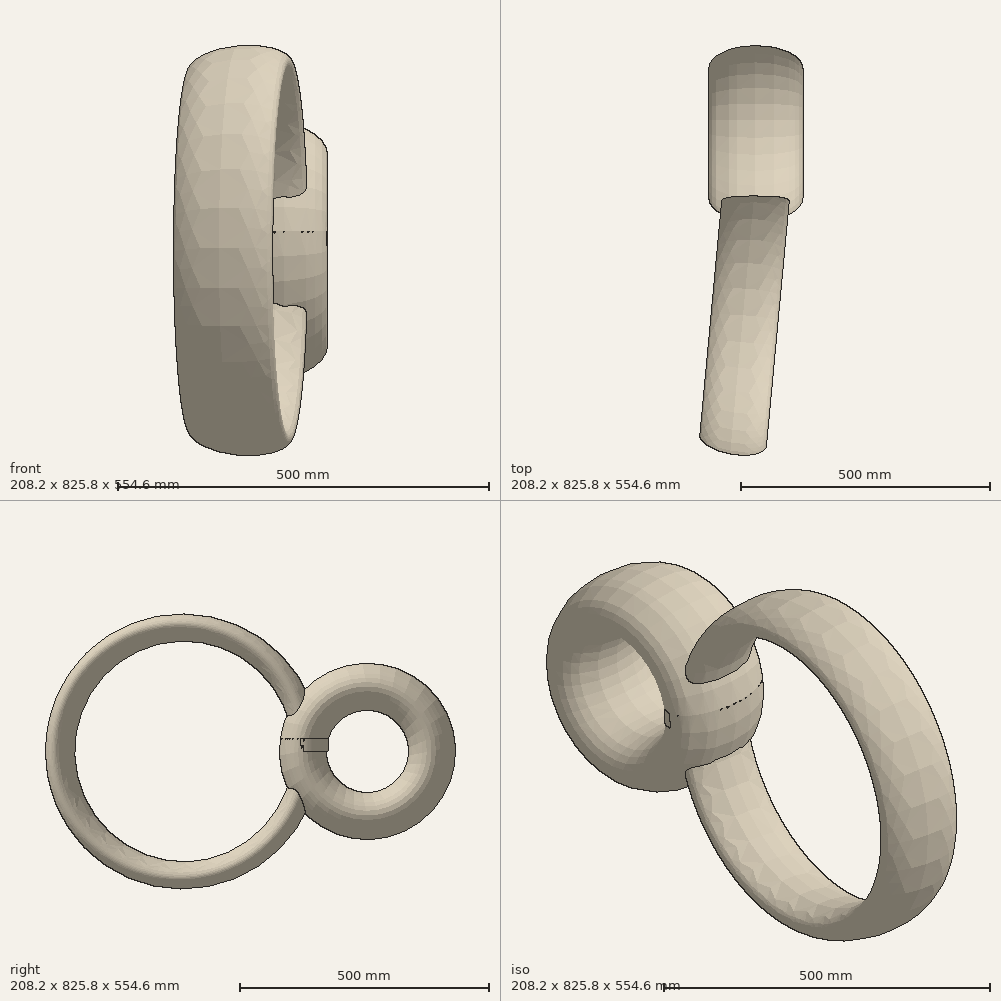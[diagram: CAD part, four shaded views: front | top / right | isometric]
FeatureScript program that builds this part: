
annotation { "Feature Type Name" : "Feature", "Feature Type Description" : "" }
export const myFeature = defineFeature(function(context is Context, id is Id, definition is map)
    precondition{}
    {
        {
            var Q0;
            Q0=qCreatedBy(makeId("Top.planeOp"),FACE);
            var sketch = newSketch(context, id + "F0", { "sketchPlane" : qUnion([Q0])});
            skEllipse(sketch, "E0", {"center": v(0, 0) * mm, "majorRadius": 95.19 * mm, "minorRadius": 48.45 * mm, "majorAxis": v(1, 0)});
            skSolve(sketch);
        }
        {
            var Q0;
            Q0 = qSketchRegion(id + "F0", true);
            extrude(context, id + "F1", {"entities" : qUnion([Q0]), "depth" : 25.4 * mm, "offsetDistance" : 25.4 * mm});
        }
        {
            var Q0;
            Q0=makeQuery(id+"F1.opExtrude","CAP_FACE",FACE,{"disambiguationData":[OSD([sQuery(id+"F0.wireOp",EDGE,"E0")])],"isStart":false});
            var sketch = newSketch(context, id + "F2", { "sketchPlane" : qUnion([Q0])});
            skEllipse(sketch, "E1", {"center": v(0, 0) * mm, "majorRadius": 68.11 * mm, "minorRadius": 27.79 * mm, "majorAxis": v(1, 0)});
            skSolve(sketch);
        }
        {
            var Q0;
            Q0 = qSketchRegion(id + "F2", true);
            extrude(context, id + "F3", {"entities" : qUnion([Q0]), "depth" : 25.4 * mm, "offsetDistance" : 25.4 * mm});
        }
        {
            var Q0;
            Q0=qCreatedBy(makeId("Top.planeOp"),FACE);
            var sketch = newSketch(context, id + "F4", { "sketchPlane" : qUnion([Q0])});
            skLineSegment(sketch, "E2", {"start": v(-155.5, 127.18) * mm, "end": v(180.45, 127.18) * mm, "construction": true});
            skSolve(sketch);
        }
        {
            var Q0;
            Q0=makeQuery(id+"F1.opExtrude","CAP_FACE",FACE,{"disambiguationData":[OSD([sQuery(id+"F0.wireOp",EDGE,"E0")])],"isStart":false});
            var Q1;
            Q1=sQuery(id+"F4.wireOp",EDGE,"E2");
            revolve(context, id + "F5", {"surfaceOperationType" : NewSurfaceOperationType.NEW, "entities" : qUnion([Q0]), "axis" : qUnion([Q1]), "revolveType" : RevolveType.FULL});
        }
        {
            var Q0;
            Q0=qCreatedBy(makeId("Top.planeOp"),FACE);
            var sketch = newSketch(context, id + "F6", { "sketchPlane" : qUnion([Q0])});
            skLineSegment(sketch, "E3", {"start": v(-262.54, -220.83) * mm, "end": v(296.74, -272.98) * mm, "construction": true});
            skSolve(sketch);
        }
        {
            var Q0;
            Q0=makeQuery(id+"F3.opExtrude","CAP_FACE",FACE,{"disambiguationData":[OSD([sQuery(id+"F2.wireOp",EDGE,"E1")])],"isStart":false});
            var Q1;
            Q1=sQuery(id+"F6.wireOp",EDGE,"E3");
            revolve(context, id + "F7", {"surfaceOperationType" : NewSurfaceOperationType.NEW, "entities" : qUnion([Q0]), "axis" : qUnion([Q1]), "revolveType" : RevolveType.FULL});
        }
    });
